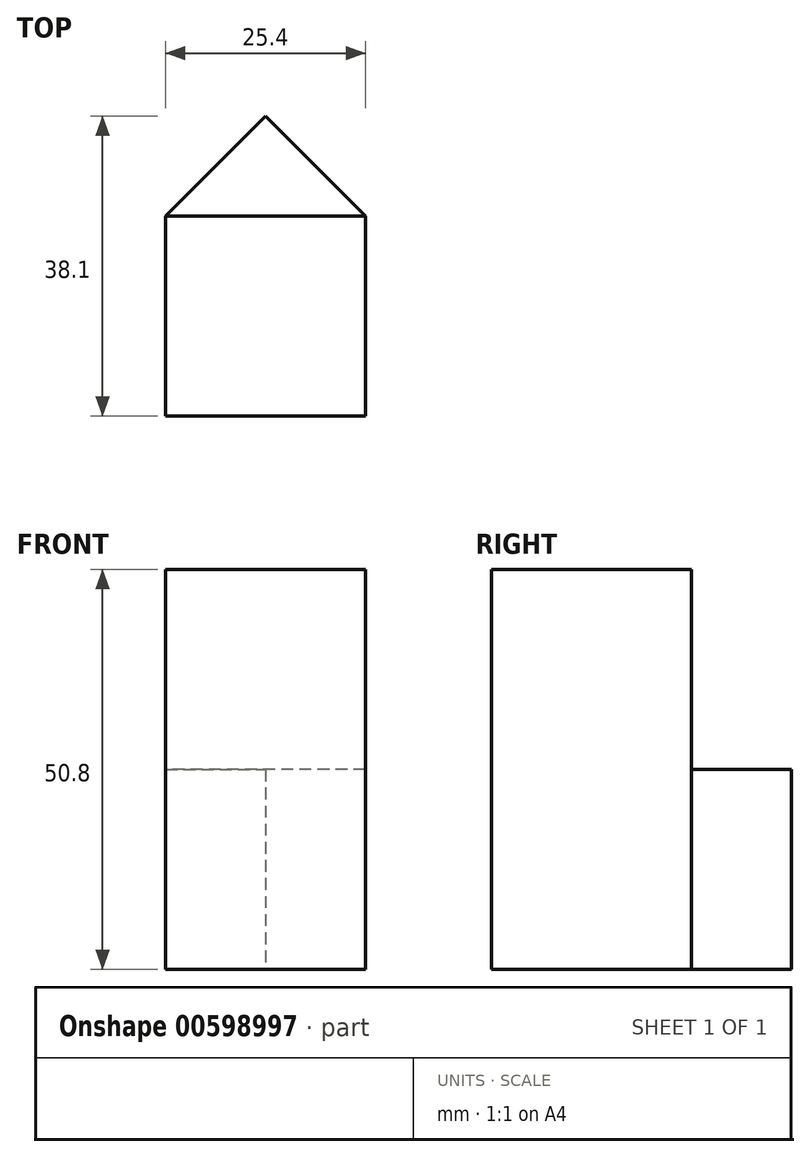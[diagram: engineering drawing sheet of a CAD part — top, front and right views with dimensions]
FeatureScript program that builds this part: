
annotation { "Feature Type Name" : "Feature", "Feature Type Description" : "" }
export const myFeature = defineFeature(function(context is Context, id is Id, definition is map)
    precondition{}
    {
        {
            var Q0;
            Q0=qCreatedBy(makeId("Top.planeOp"),FACE);
            var sketch = newSketch(context, id + "F0", { "sketchPlane" : qUnion([Q0])});
            skLineSegment(sketch, "E0.bottom", {"start": v(12.7, 12.7) * mm, "end": v(-12.7, 12.7) * mm});
            skLineSegment(sketch, "E0.top", {"start": v(12.7, -12.7) * mm, "end": v(-12.7, -12.7) * mm});
            skLineSegment(sketch, "E0.left", {"start": v(12.7, 12.7) * mm, "end": v(12.7, -12.7) * mm});
            skLineSegment(sketch, "E0.right", {"start": v(-12.7, 12.7) * mm, "end": v(-12.7, -12.7) * mm});
            skPoint(sketch, "E0.middle", {"position": v(0, 0) * mm});
            skLineSegment(sketch, "E1", {"start": v(-12.7, 12.7) * mm, "end": v(0, 25.4) * mm});
            skLineSegment(sketch, "E2", {"start": v(12.7, 12.7) * mm, "end": v(0, 25.4) * mm});
            skSolve(sketch);
        }
        {
            var Q0;
            Q0=makeQuery(id+"F0.imprint","IMPRINT",FACE,{"disambiguationData":[TD([[makeQuery(id+"F0.imprint","IMPRINT",EDGE,{"derivedFrom":sQuery(id+"F0.wireOp",EDGE,"E0.bottom")}),-1.0]])]});
            extrude(context, id + "F1", {"entities" : qUnion([Q0]), "depth" : 25.4 * mm, "offsetDistance" : 25.4 * mm});
        }
        {
            var Q0;
            Q0=makeQuery(id+"F0.imprint","IMPRINT",FACE,{"disambiguationData":[TD([[makeQuery(id+"F0.imprint","IMPRINT",EDGE,{"derivedFrom":sQuery(id+"F0.wireOp",EDGE,"E0.bottom")}),1.0]])]});
            extrude(context, id + "F2", {"entities" : qUnion([Q0]), "operationType" : NewBodyOperationType.ADD, "depth" : 50.8 * mm, "offsetDistance" : 25.4 * mm});
        }
    });
